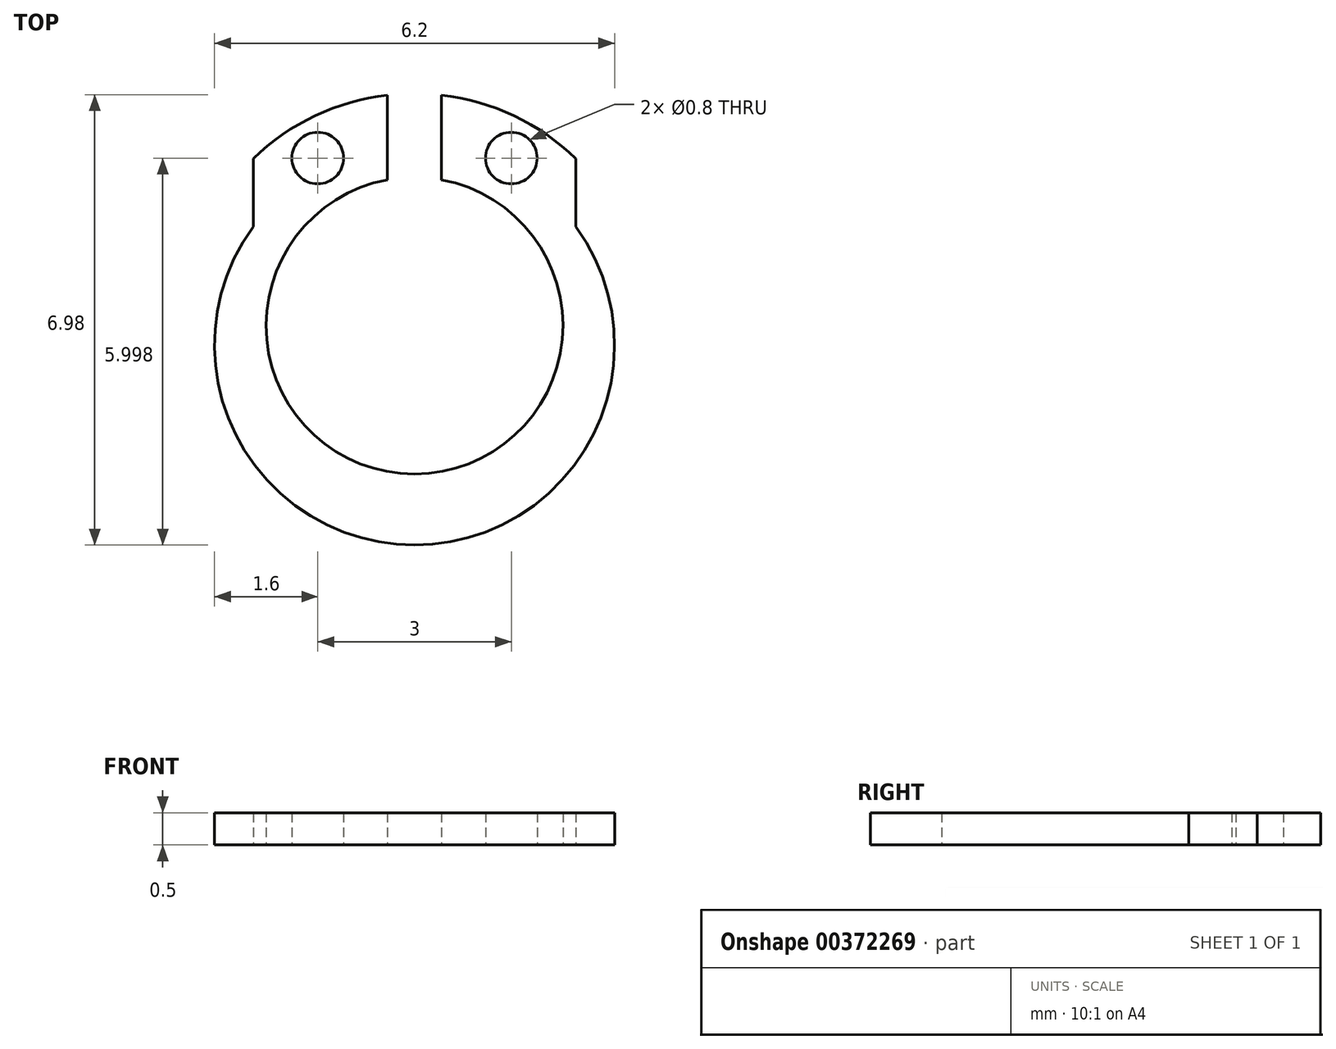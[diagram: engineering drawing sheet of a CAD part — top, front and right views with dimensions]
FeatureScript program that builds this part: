
annotation { "Feature Type Name" : "Feature", "Feature Type Description" : "" }
export const myFeature = defineFeature(function(context is Context, id is Id, definition is map)
    precondition{}
    {
        {
            var Q0;
            Q0=qCreatedBy(makeId("Top.planeOp"),FACE);
            var sketch = newSketch(context, id + "F0", { "sketchPlane" : qUnion([Q0])});
            skCircle(sketch, "E0", {"center": v(0, 0) * mm, "radius": 3 * mm, "construction": true});
            skArc(sketch, "E1", {"start": v(2.5, 2.6) * mm, "mid": v(1.54, 3.25) * mm, "end": v(0.42, 3.58) * mm});
            skArc(sketch, "E2", {"start": v(-0.42, 2.26) * mm, "mid": v(0, -2.3) * mm, "end": v(0.42, 2.26) * mm});
            skCircle(sketch, "E3", {"center": v(-1.5, 2.6) * mm, "radius": 0.4 * mm});
            skCircle(sketch, "E4", {"center": v(1.5, 2.6) * mm, "radius": 0.4 * mm});
            skLineSegment(sketch, "E5", {"start": v(-0.42, 3.58) * mm, "end": v(-0.42, 2.26) * mm});
            skLineSegment(sketch, "E6", {"start": v(0.42, 3.58) * mm, "end": v(0.42, 2.26) * mm});
            skLineSegment(sketch, "E7", {"start": v(-2.5, 2.6) * mm, "end": v(-2.5, 1.53) * mm});
            skLineSegment(sketch, "E8", {"start": v(2.5, 2.6) * mm, "end": v(2.5, 1.53) * mm});
            skArc(sketch, "E9.trimOffspring", {"start": v(-0.42, 3.58) * mm, "mid": v(-1.54, 3.25) * mm, "end": v(-2.5, 2.6) * mm});
            skArc(sketch, "E10.trimOffspring", {"start": v(-2.5, 1.53) * mm, "mid": v(0, -3.4) * mm, "end": v(2.5, 1.53) * mm});
            skSolve(sketch);
        }
        {
            var Q0;
            Q0=makeQuery(id+"F0.imprint","IMPRINT",FACE,{"disambiguationData":[TD([[makeQuery(id+"F0.imprint","IMPRINT",EDGE,{"derivedFrom":sQuery(id+"F0.wireOp",EDGE,"E1")}),1.0]])]});
            extrude(context, id + "F1", {"entities" : qUnion([Q0]), "depth" : 0.5 * mm});
        }
    });
